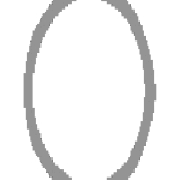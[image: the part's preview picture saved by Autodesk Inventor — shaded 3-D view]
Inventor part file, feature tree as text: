
AUTODESK INVENTOR PART (.ipt)
format: ipt  version: 2021 (Build 250183000, 183)  size: 148,480 bytes
history: native  units: in
note: dims shown in document units (in); Inventor stores cm internally (conversion verified against a paired STEP export)
features: other x5, sketch x2, sweep x1, plane x1
ambient origin geometry x8: Origin, YZ Plane, XZ Plane, XY Plane, X Axis, Y Axis, Z Axis, Center Point
bodies: Solid1 (feature_tree), Body (feature_tree)
feature tree (9):
  other  "Driven Length"
  other  "Frame Generator"
  other  "Start Plane"
  other  "End Plane"
  sweep  "Sweep Path"
  other  "Orientation Work Plane"
  sketch  "Sketch2"  dims[d0=1.0in d1=0.065in]
  plane  "Work Plane3"
  sketch  "Sketch3"  dims[d2=1.1738in d4=-0.0in d5=1.1738in d8=90.0deg d9=1.1738in d10=0.0in d11=0.0in]
